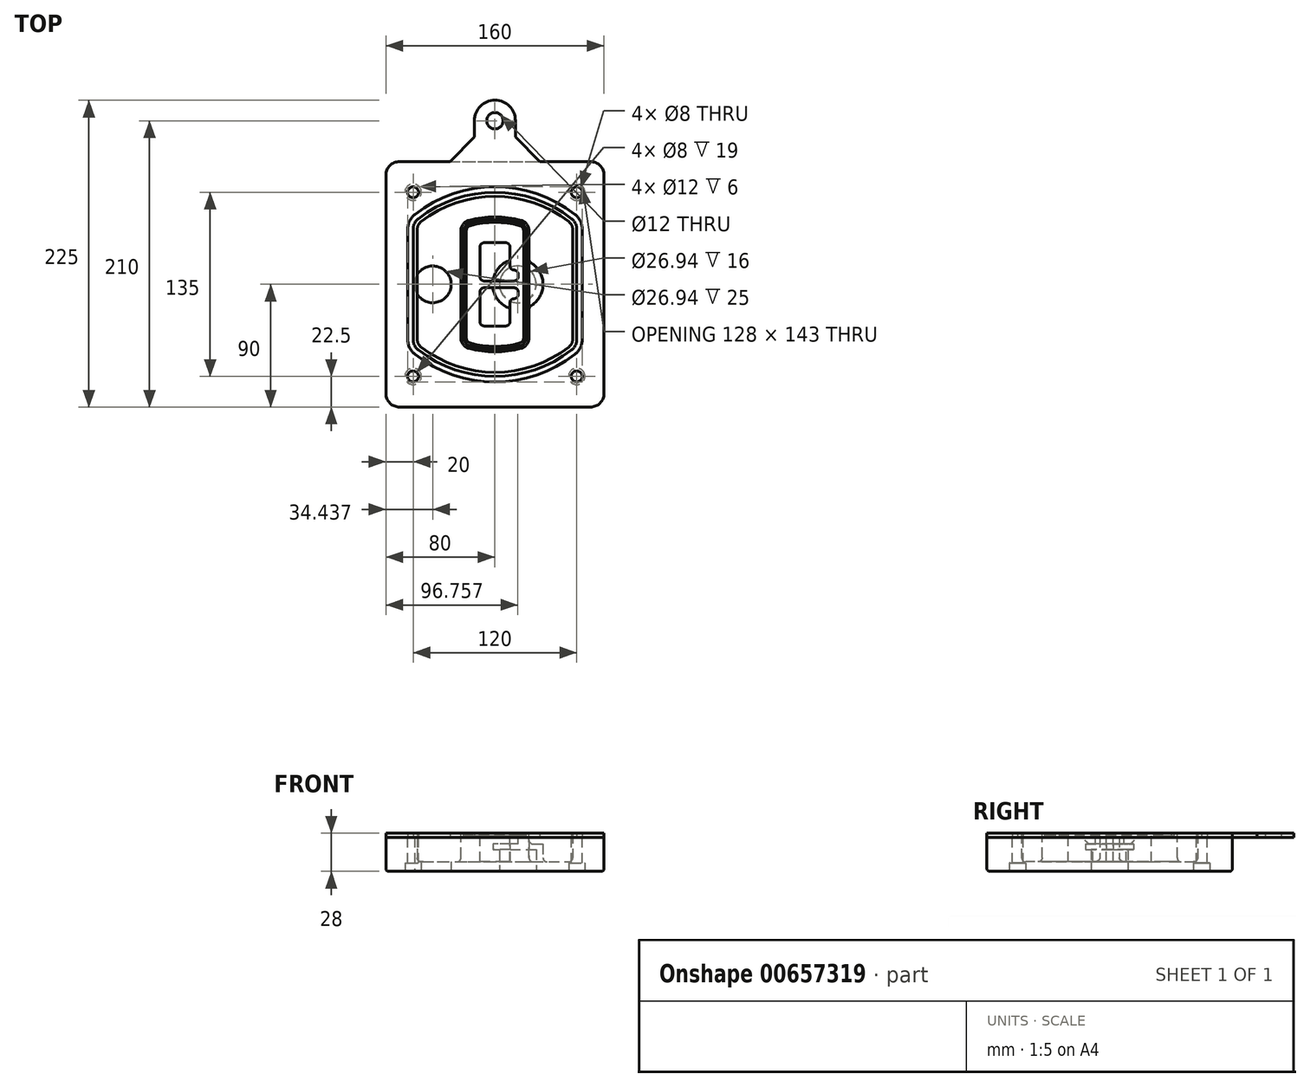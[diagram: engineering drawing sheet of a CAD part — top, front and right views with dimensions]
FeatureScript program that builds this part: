
annotation { "Feature Type Name" : "Feature", "Feature Type Description" : "" }
export const myFeature = defineFeature(function(context is Context, id is Id, definition is map)
    precondition{}
    {
        {
            var Q0;
            Q0=qCreatedBy(makeId("Top.planeOp"),FACE);
            var sketch = newSketch(context, id + "F0", { "sketchPlane" : qUnion([Q0])});
            skPoint(sketch, "E0.rect.middle", {"position": v(0, 0) * mm});
            skLineSegment(sketch, "E1.bottom", {"start": v(-70, -90) * mm, "end": v(70, -90) * mm});
            skLineSegment(sketch, "E1.top", {"start": v(-70, 90) * mm, "end": v(70, 90) * mm});
            skLineSegment(sketch, "E1.left", {"start": v(-80, -80) * mm, "end": v(-80, 80) * mm});
            skLineSegment(sketch, "E1.right", {"start": v(80, -80) * mm, "end": v(80, 80) * mm});
            skLineSegment(sketch, "E2", {"start": v(-80, 90) * mm, "end": v(80, -90) * mm, "construction": true});
            skLineSegment(sketch, "E3", {"start": v(80, 90) * mm, "end": v(-80, -90) * mm, "construction": true});
            skCircle(sketch, "E4", {"center": v(-60, 67.5) * mm, "radius": 4 * mm});
            skCircle(sketch, "E5", {"center": v(60, 67.5) * mm, "radius": 4 * mm});
            skCircle(sketch, "E6", {"center": v(60, -67.5) * mm, "radius": 4 * mm});
            skCircle(sketch, "E7", {"center": v(-60, -67.5) * mm, "radius": 4 * mm});
            skLineSegment(sketch, "E8", {"start": v(-60, 67.5) * mm, "end": v(60, 67.5) * mm, "construction": true});
            skLineSegment(sketch, "E9", {"start": v(60, 67.5) * mm, "end": v(60, -67.5) * mm, "construction": true});
            skLineSegment(sketch, "E10", {"start": v(60, -67.5) * mm, "end": v(-60, -67.5) * mm, "construction": true});
            skLineSegment(sketch, "E11", {"start": v(-60, -67.5) * mm, "end": v(-60, 67.5) * mm, "construction": true});
            skLineSegment(sketch, "E12", {"start": v(-60, 40.3) * mm, "end": v(-60, -40.3) * mm});
            skLineSegment(sketch, "E13", {"start": v(60, 40.3) * mm, "end": v(60, -40.3) * mm});
            skArc(sketch, "E14", {"start": v(56.15, 48.18) * mm, "mid": v(0, 67.5) * mm, "end": v(-56.15, 48.18) * mm});
            skArc(sketch, "E15", {"start": v(-56.15, -48.18) * mm, "mid": v(0, -67.5) * mm, "end": v(56.15, -48.18) * mm});
            skLineSegment(sketch, "E16", {"start": v(-60, 0) * mm, "end": v(60, 0) * mm, "construction": true});
            skPoint(sketch, "E17.visualSharp", {"position": v(-60, -45) * mm});
            skArc(sketch, "E17.filletArc", {"start": v(-60, -40.3) * mm, "mid": v(-58.99, -44.68) * mm, "end": v(-56.15, -48.18) * mm});
            skPoint(sketch, "E18.visualSharp", {"position": v(-60, 45) * mm});
            skArc(sketch, "E18.filletArc", {"start": v(-56.15, 48.18) * mm, "mid": v(-58.99, 44.68) * mm, "end": v(-60, 40.3) * mm});
            skPoint(sketch, "E19.visualSharp", {"position": v(60, 45) * mm});
            skArc(sketch, "E19.filletArc", {"start": v(60, 40.3) * mm, "mid": v(58.99, 44.68) * mm, "end": v(56.15, 48.18) * mm});
            skPoint(sketch, "E20.visualSharp", {"position": v(60, -45) * mm});
            skArc(sketch, "E20.filletArc", {"start": v(56.15, -48.18) * mm, "mid": v(58.99, -44.68) * mm, "end": v(60, -40.3) * mm});
            skPoint(sketch, "E21.visualSharp", {"position": v(-80, 90) * mm});
            skArc(sketch, "E21.filletArc", {"start": v(-70, 90) * mm, "mid": v(-77.07, 87.07) * mm, "end": v(-80, 80) * mm});
            skPoint(sketch, "E22.visualSharp", {"position": v(80, 90) * mm});
            skArc(sketch, "E22.filletArc", {"start": v(80, 80) * mm, "mid": v(77.07, 87.07) * mm, "end": v(70, 90) * mm});
            skPoint(sketch, "E23.visualSharp", {"position": v(80, -90) * mm});
            skArc(sketch, "E23.filletArc", {"start": v(70, -90) * mm, "mid": v(77.07, -87.07) * mm, "end": v(80, -80) * mm});
            skPoint(sketch, "E24.visualSharp", {"position": v(-80, -90) * mm});
            skArc(sketch, "E24.filletArc", {"start": v(-80, -80) * mm, "mid": v(-77.07, -87.07) * mm, "end": v(-70, -90) * mm});
            skArc(sketch, "E25.0", {"start": v(57, 40.3) * mm, "mid": v(56.3, 43.36) * mm, "end": v(54.3, 45.81) * mm});
            skLineSegment(sketch, "E25.1", {"start": v(57, 40.3) * mm, "end": v(57, -40.3) * mm});
            skArc(sketch, "E25.2", {"start": v(54.3, -45.81) * mm, "mid": v(56.3, -43.36) * mm, "end": v(57, -40.3) * mm});
            skArc(sketch, "E25.3", {"start": v(-54.3, -45.81) * mm, "mid": v(0, -64.5) * mm, "end": v(54.3, -45.81) * mm});
            skArc(sketch, "E25.4", {"start": v(-57, -40.3) * mm, "mid": v(-56.3, -43.36) * mm, "end": v(-54.3, -45.81) * mm});
            skArc(sketch, "E25.5", {"start": v(54.3, 45.81) * mm, "mid": v(0, 64.5) * mm, "end": v(-54.3, 45.81) * mm});
            skLineSegment(sketch, "E25.6", {"start": v(-57, 40.3) * mm, "end": v(-57, -40.3) * mm});
            skArc(sketch, "E25.7", {"start": v(-54.3, 45.81) * mm, "mid": v(-56.3, 43.36) * mm, "end": v(-57, 40.3) * mm});
            skArc(sketch, "E26.0", {"start": v(-58.62, 51.33) * mm, "mid": v(-62.58, 46.43) * mm, "end": v(-64, 40.3) * mm});
            skArc(sketch, "E26.1", {"start": v(58.62, 51.33) * mm, "mid": v(0, 71.5) * mm, "end": v(-58.62, 51.33) * mm});
            skArc(sketch, "E26.2", {"start": v(64, 40.3) * mm, "mid": v(62.58, 46.43) * mm, "end": v(58.62, 51.33) * mm});
            skLineSegment(sketch, "E26.3", {"start": v(64, 40.3) * mm, "end": v(64, -40.3) * mm});
            skArc(sketch, "E26.4", {"start": v(58.62, -51.33) * mm, "mid": v(62.58, -46.43) * mm, "end": v(64, -40.3) * mm});
            skLineSegment(sketch, "E26.5", {"start": v(-64, 40.3) * mm, "end": v(-64, -40.3) * mm});
            skArc(sketch, "E26.6", {"start": v(-58.62, -51.33) * mm, "mid": v(0, -71.5) * mm, "end": v(58.62, -51.33) * mm});
            skArc(sketch, "E26.7", {"start": v(-64, -40.3) * mm, "mid": v(-62.58, -46.43) * mm, "end": v(-58.62, -51.33) * mm});
            skLineSegment(sketch, "E27", {"start": v(0, 90) * mm, "end": v(0, 120) * mm, "construction": true});
            skCircle(sketch, "E28", {"center": v(0, 120) * mm, "radius": 6 * mm});
            skLineSegment(sketch, "E29", {"start": v(-33, 90) * mm, "end": v(-15, 108) * mm});
            skLineSegment(sketch, "E30", {"start": v(33, 90) * mm, "end": v(15, 108) * mm});
            skLineSegment(sketch, "E31", {"start": v(-15, 108) * mm, "end": v(-15, 120) * mm});
            skLineSegment(sketch, "E32", {"start": v(15, 108) * mm, "end": v(15, 120) * mm});
            skArc(sketch, "E33", {"start": v(15, 120) * mm, "mid": v(0, 135) * mm, "end": v(-15, 120) * mm});
            skLineSegment(sketch, "E34", {"start": v(-80, 0) * mm, "end": v(80, 0) * mm, "construction": true});
            skSolve(sketch);
        }
        {
            var Q0;
            Q0=makeQuery(id+"F0.imprint","IMPRINT",FACE,{"disambiguationData":[TD([[makeQuery(id+"F0.imprint","IMPRINT",EDGE,{"derivedFrom":sQuery(id+"F0.wireOp",EDGE,"E1.bottom")}),1.0]])]});
            var Q1;
            Q1=makeQuery(id+"F0.imprint","IMPRINT",FACE,{"disambiguationData":[TD([[makeQuery(id+"F0.imprint","IMPRINT",EDGE,{"derivedFrom":sQuery(id+"F0.wireOp",EDGE,"E12")}),1.0]])]});
            var Q2;
            Q2=makeQuery(id+"F0.imprint","IMPRINT",FACE,{"disambiguationData":[TD([[makeQuery(id+"F0.imprint","IMPRINT",EDGE,{"derivedFrom":sQuery(id+"F0.wireOp",EDGE,"E25.0")}),1.0]])]});
            var Q3;
            Q3=makeQuery(id+"F0.imprint","IMPRINT",FACE,{"disambiguationData":[TD([[makeQuery(id+"F0.imprint","IMPRINT",EDGE,{"derivedFrom":sQuery(id+"F0.wireOp",EDGE,"E12")}),-1.0]])]});
            extrude(context, id + "F1", {"entities" : qUnion([Q0, Q1, Q2, Q3]), "oppositeDirection" : true, "depth" : 25 * mm});
        }
        {
            var Q0;
            Q0=makeQuery(id+"F0.imprint","IMPRINT",FACE,{"disambiguationData":[TD([[makeQuery(id+"F0.imprint","IMPRINT",EDGE,{"derivedFrom":sQuery(id+"F0.wireOp",EDGE,"E12")}),1.0]])]});
            extrude(context, id + "F2", {"entities" : qUnion([Q0]), "operationType" : NewBodyOperationType.ADD, "depth" : 3 * mm});
        }
        {
            var Q0;
            Q0=makeQuery(id+"F0.imprint","IMPRINT",FACE,{"disambiguationData":[TD([[makeQuery(id+"F0.imprint","IMPRINT",EDGE,{"derivedFrom":sQuery(id+"F0.wireOp",EDGE,"E25.0")}),1.0]])]});
            extrude(context, id + "F3", {"entities" : qUnion([Q0]), "operationType" : NewBodyOperationType.REMOVE, "oppositeDirection" : true, "depth" : 18 * mm});
        }
        {
            var Q0;
            Q0=makeQuery(id+"F2.opExtrude","CAP_FACE",FACE,{"disambiguationData":[OSD([sQuery(id+"F0.wireOp",EDGE,"E12"),sQuery(id+"F0.wireOp",EDGE,"E13"),sQuery(id+"F0.wireOp",EDGE,"E14"),sQuery(id+"F0.wireOp",EDGE,"E15"),sQuery(id+"F0.wireOp",EDGE,"E17.filletArc"),sQuery(id+"F0.wireOp",EDGE,"E18.filletArc"),sQuery(id+"F0.wireOp",EDGE,"E19.filletArc"),sQuery(id+"F0.wireOp",EDGE,"E20.filletArc"),sQuery(id+"F0.wireOp",EDGE,"E25.0"),sQuery(id+"F0.wireOp",EDGE,"E25.1"),sQuery(id+"F0.wireOp",EDGE,"E25.2"),sQuery(id+"F0.wireOp",EDGE,"E25.3"),sQuery(id+"F0.wireOp",EDGE,"E25.4"),sQuery(id+"F0.wireOp",EDGE,"E25.5"),sQuery(id+"F0.wireOp",EDGE,"E25.6"),sQuery(id+"F0.wireOp",EDGE,"E25.7")])],"isStart":false});
            var sketch = newSketch(context, id + "F4", { "sketchPlane" : qUnion([Q0])});
            skArc(sketch, "E35.0", {"start": v(-19.08, -46.97) * mm, "mid": v(0, -49.5) * mm, "end": v(19.08, -46.97) * mm});
            skArc(sketch, "E36.0", {"start": v(19.08, 46.97) * mm, "mid": v(0, 49.5) * mm, "end": v(-19.08, 46.97) * mm});
            skLineSegment(sketch, "E37", {"start": v(-25, 39.25) * mm, "end": v(-25, -39.25) * mm});
            skLineSegment(sketch, "E38", {"start": v(25, 39.25) * mm, "end": v(25, -39.25) * mm});
            skLineSegment(sketch, "E39", {"start": v(-25, 45.1) * mm, "end": v(25, 45.1) * mm, "construction": true});
            skLineSegment(sketch, "E40", {"start": v(-25, -45.1) * mm, "end": v(25, -45.1) * mm, "construction": true});
            skPoint(sketch, "E41.visualSharp", {"position": v(-25, 45.1) * mm});
            skArc(sketch, "E41.filletArc", {"start": v(-19.08, 46.97) * mm, "mid": v(-23.35, 44.11) * mm, "end": v(-25, 39.25) * mm});
            skPoint(sketch, "E42.visualSharp", {"position": v(25, 45.1) * mm});
            skArc(sketch, "E42.filletArc", {"start": v(25, 39.25) * mm, "mid": v(23.35, 44.11) * mm, "end": v(19.08, 46.97) * mm});
            skPoint(sketch, "E43.visualSharp", {"position": v(25, -45.1) * mm});
            skArc(sketch, "E43.filletArc", {"start": v(19.08, -46.97) * mm, "mid": v(23.35, -44.11) * mm, "end": v(25, -39.25) * mm});
            skPoint(sketch, "E44.visualSharp", {"position": v(-25, -45.1) * mm});
            skArc(sketch, "E44.filletArc", {"start": v(-25, -39.25) * mm, "mid": v(-23.35, -44.11) * mm, "end": v(-19.08, -46.97) * mm});
            skArc(sketch, "E45.0", {"start": v(54.3, 45.81) * mm, "mid": v(0, 64.5) * mm, "end": v(-54.3, 45.81) * mm});
            skArc(sketch, "E45.1", {"start": v(-54.3, 45.81) * mm, "mid": v(-56.3, 43.36) * mm, "end": v(-57, 40.3) * mm});
            skLineSegment(sketch, "E45.2", {"start": v(-57, 40.3) * mm, "end": v(-57, -40.3) * mm});
            skArc(sketch, "E45.3", {"start": v(-57, -40.3) * mm, "mid": v(-56.3, -43.36) * mm, "end": v(-54.3, -45.81) * mm});
            skArc(sketch, "E45.4", {"start": v(-54.3, -45.81) * mm, "mid": v(0, -64.5) * mm, "end": v(54.3, -45.81) * mm});
            skArc(sketch, "E45.5", {"start": v(54.3, -45.81) * mm, "mid": v(56.3, -43.36) * mm, "end": v(57, -40.3) * mm});
            skLineSegment(sketch, "E45.6", {"start": v(57, 40.3) * mm, "end": v(57, -40.3) * mm});
            skArc(sketch, "E45.7", {"start": v(57, 40.3) * mm, "mid": v(56.3, 43.36) * mm, "end": v(54.3, 45.81) * mm});
            skLineSegment(sketch, "E46.0", {"start": v(23, 39.25) * mm, "end": v(23, -39.25) * mm});
            skArc(sketch, "E46.1", {"start": v(18.56, -45.04) * mm, "mid": v(21.76, -42.9) * mm, "end": v(23, -39.25) * mm});
            skArc(sketch, "E46.2", {"start": v(-18.56, -45.04) * mm, "mid": v(0, -47.5) * mm, "end": v(18.56, -45.04) * mm});
            skArc(sketch, "E46.3", {"start": v(-23, -39.25) * mm, "mid": v(-21.76, -42.9) * mm, "end": v(-18.56, -45.04) * mm});
            skLineSegment(sketch, "E46.4", {"start": v(-23, 39.25) * mm, "end": v(-23, -39.25) * mm});
            skArc(sketch, "E46.5", {"start": v(23, 39.25) * mm, "mid": v(21.76, 42.9) * mm, "end": v(18.56, 45.04) * mm});
            skArc(sketch, "E46.6", {"start": v(-18.56, 45.04) * mm, "mid": v(-21.76, 42.9) * mm, "end": v(-23, 39.25) * mm});
            skArc(sketch, "E46.7", {"start": v(18.56, 45.04) * mm, "mid": v(0, 47.5) * mm, "end": v(-18.56, 45.04) * mm});
            skArc(sketch, "E47.0", {"start": v(21, 39.25) * mm, "mid": v(20.18, 41.68) * mm, "end": v(18.04, 43.1) * mm});
            skLineSegment(sketch, "E47.1", {"start": v(21, 39.25) * mm, "end": v(21, -39.25) * mm});
            skArc(sketch, "E47.2", {"start": v(18.04, -43.1) * mm, "mid": v(20.18, -41.68) * mm, "end": v(21, -39.25) * mm});
            skArc(sketch, "E47.3", {"start": v(-18.04, -43.1) * mm, "mid": v(0, -45.5) * mm, "end": v(18.04, -43.1) * mm});
            skArc(sketch, "E47.4", {"start": v(-21, -39.25) * mm, "mid": v(-20.18, -41.68) * mm, "end": v(-18.04, -43.1) * mm});
            skArc(sketch, "E47.5", {"start": v(18.04, 43.1) * mm, "mid": v(0, 45.5) * mm, "end": v(-18.04, 43.1) * mm});
            skLineSegment(sketch, "E47.6", {"start": v(-21, 39.25) * mm, "end": v(-21, -39.25) * mm});
            skArc(sketch, "E47.7", {"start": v(-18.04, 43.1) * mm, "mid": v(-20.18, 41.68) * mm, "end": v(-21, 39.25) * mm});
            skLineSegment(sketch, "E48", {"start": v(-25, 0) * mm, "end": v(25, 0) * mm, "construction": true});
            skLineSegment(sketch, "E49", {"start": v(-11, 5.5) * mm, "end": v(-11, 27.5) * mm});
            skLineSegment(sketch, "E50", {"start": v(-8, 30.5) * mm, "end": v(8, 30.5) * mm});
            skLineSegment(sketch, "E51", {"start": v(11, 27.5) * mm, "end": v(11, 13.5) * mm});
            skLineSegment(sketch, "E52", {"start": v(14, 10.5) * mm, "end": v(14, 10.5) * mm});
            skLineSegment(sketch, "E53", {"start": v(17, 7.5) * mm, "end": v(17, 5.5) * mm});
            skLineSegment(sketch, "E54", {"start": v(14, 2.5) * mm, "end": v(-8, 2.5) * mm});
            skPoint(sketch, "E55.visualSharp", {"position": v(-11, 30.5) * mm});
            skArc(sketch, "E55.filletArc", {"start": v(-8, 30.5) * mm, "mid": v(-10.12, 29.62) * mm, "end": v(-11, 27.5) * mm});
            skPoint(sketch, "E56.visualSharp", {"position": v(11, 30.5) * mm});
            skArc(sketch, "E56.filletArc", {"start": v(11, 27.5) * mm, "mid": v(10.12, 29.62) * mm, "end": v(8, 30.5) * mm});
            skPoint(sketch, "E57.visualSharp", {"position": v(11, 10.5) * mm});
            skArc(sketch, "E57.filletArc", {"start": v(11, 13.5) * mm, "mid": v(11.88, 11.38) * mm, "end": v(14, 10.5) * mm});
            skPoint(sketch, "E58.visualSharp", {"position": v(17, 10.5) * mm});
            skArc(sketch, "E58.filletArc", {"start": v(17, 7.5) * mm, "mid": v(16.12, 9.62) * mm, "end": v(14, 10.5) * mm});
            skPoint(sketch, "E59.visualSharp", {"position": v(17, 2.5) * mm});
            skArc(sketch, "E59.filletArc", {"start": v(14, 2.5) * mm, "mid": v(16.12, 3.38) * mm, "end": v(17, 5.5) * mm});
            skPoint(sketch, "E60.visualSharp", {"position": v(-11, 2.5) * mm});
            skArc(sketch, "E60.filletArc", {"start": v(-11, 5.5) * mm, "mid": v(-10.12, 3.38) * mm, "end": v(-8, 2.5) * mm});
            skLineSegment(sketch, "E61.0.MirrorCS", {"start": v(14, -2.5) * mm, "end": v(-8, -2.5) * mm});
            skArc(sketch, "E62.0.MirrorCS", {"start": v(-11, -5.5) * mm, "mid": v(-10.12, -3.38) * mm, "end": v(-8, -2.5) * mm});
            skLineSegment(sketch, "E63.0.MirrorCS", {"start": v(-11, -5.5) * mm, "end": v(-11, -27.5) * mm});
            skArc(sketch, "E64.0.MirrorCS", {"start": v(-8, -30.5) * mm, "mid": v(-10.12, -29.62) * mm, "end": v(-11, -27.5) * mm});
            skLineSegment(sketch, "E65.0.MirrorCS", {"start": v(-8, -30.5) * mm, "end": v(8, -30.5) * mm});
            skArc(sketch, "E66.0.MirrorCS", {"start": v(11, -27.5) * mm, "mid": v(10.12, -29.62) * mm, "end": v(8, -30.5) * mm});
            skLineSegment(sketch, "E67.0.MirrorCS", {"start": v(11, -27.5) * mm, "end": v(11, -13.5) * mm});
            skArc(sketch, "E68.0.MirrorCS", {"start": v(11, -13.5) * mm, "mid": v(11.88, -11.38) * mm, "end": v(14, -10.5) * mm});
            skArc(sketch, "E69.0.MirrorCS", {"start": v(17, -7.5) * mm, "mid": v(16.12, -9.62) * mm, "end": v(14, -10.5) * mm});
            skLineSegment(sketch, "E70.0.MirrorCS", {"start": v(17, -7.5) * mm, "end": v(17, -5.5) * mm});
            skArc(sketch, "E71.0.MirrorCS", {"start": v(14, -2.5) * mm, "mid": v(16.12, -3.38) * mm, "end": v(17, -5.5) * mm});
            skSolve(sketch);
        }
        {
            var Q0;
            Q0=makeQuery(id+"F4.imprint","IMPRINT",FACE,{"disambiguationData":[TD([[makeQuery(id+"F4.imprint","IMPRINT",EDGE,{"derivedFrom":sQuery(id+"F4.wireOp",EDGE,"E35.0")}),1.0]])]});
            var Q1;
            Q1=makeQuery(id+"F4.imprint","IMPRINT",FACE,{"disambiguationData":[TD([[makeQuery(id+"F4.imprint","IMPRINT",EDGE,{"derivedFrom":sQuery(id+"F4.wireOp",EDGE,"E46.0")}),-1.0]])]});
            var Q2;
            Q2=makeQuery(id+"F4.imprint","IMPRINT",FACE,{"disambiguationData":[TD([[makeQuery(id+"F4.imprint","IMPRINT",EDGE,{"derivedFrom":sQuery(id+"F4.wireOp",EDGE,"E47.0")}),1.0]])]});
            extrude(context, id + "F5", {"entities" : qUnion([Q0, Q1, Q2]), "operationType" : NewBodyOperationType.ADD, "endBound" : BoundingType.UP_TO_NEXT, "oppositeDirection" : true, "depth" : 25 * mm});
        }
        {
            var Q0;
            Q0=makeQuery(id+"F4.imprint","IMPRINT",FACE,{"disambiguationData":[TD([[makeQuery(id+"F4.imprint","IMPRINT",EDGE,{"derivedFrom":sQuery(id+"F4.wireOp",EDGE,"E46.0")}),-1.0]])]});
            extrude(context, id + "F6", {"entities" : qUnion([Q0]), "operationType" : NewBodyOperationType.REMOVE, "oppositeDirection" : true, "depth" : 2 * mm});
        }
        {
            var Q0;
            Q0=makeQuery(id+"F1.opExtrude","CAP_FACE",FACE,{"disambiguationData":[OSD([sQuery(id+"F0.wireOp",EDGE,"E1.bottom"),sQuery(id+"F0.wireOp",EDGE,"E1.top"),sQuery(id+"F0.wireOp",EDGE,"E1.left"),sQuery(id+"F0.wireOp",EDGE,"E1.right"),sQuery(id+"F0.wireOp",EDGE,"E4"),sQuery(id+"F0.wireOp",EDGE,"E5"),sQuery(id+"F0.wireOp",EDGE,"E6"),sQuery(id+"F0.wireOp",EDGE,"E7"),sQuery(id+"F0.wireOp",EDGE,"E21.filletArc"),sQuery(id+"F0.wireOp",EDGE,"E22.filletArc"),sQuery(id+"F0.wireOp",EDGE,"E23.filletArc"),sQuery(id+"F0.wireOp",EDGE,"E24.filletArc")])],"isStart":false});
            var sketch = newSketch(context, id + "F7", { "sketchPlane" : qUnion([Q0])});
            skCircle(sketch, "E72", {"center": v(16.76, 0) * mm, "radius": 13.47 * mm});
            skCircle(sketch, "E73", {"center": v(-45.56, 0) * mm, "radius": 13.47 * mm});
            skLineSegment(sketch, "E74", {"start": v(80, 0) * mm, "end": v(-80, 0) * mm});
            skCircle(sketch, "E75", {"center": v(16.76, 0) * mm, "radius": 18.47 * mm});
            skCircle(sketch, "E76", {"center": v(60, -67.5) * mm, "radius": 6 * mm});
            skCircle(sketch, "E77", {"center": v(-60, -67.5) * mm, "radius": 6 * mm});
            skCircle(sketch, "E78", {"center": v(-60, 67.5) * mm, "radius": 6 * mm});
            skCircle(sketch, "E79", {"center": v(60, 67.5) * mm, "radius": 6 * mm});
            skSolve(sketch);
        }
        {
            var Q0;
            {var subQ1=sQuery(id+"F7.wireOp",EDGE,"E74");var subQ4=sQuery(id+"F7.wireOp",EDGE,"E72");var subQ6=makeQuery(id+"F7.imprint","INTERSECT",VERTEX,{"disambiguationData":[OD(0.0)],"derivedFrom":[subQ4,subQ1]});Q0=makeQuery(id+"F7.imprint","IMPRINT",FACE,{"disambiguationData":[TD([[makeQuery(id+"F7.imprint","IMPRINT",EDGE,{"disambiguationData":[TD([[subQ6,-1.0]])],"derivedFrom":subQ4}),-1.0]])]});}
            var Q1;
            {var subQ0=sQuery(id+"F7.wireOp",EDGE,"E74");var subQ1=sQuery(id+"F7.wireOp",EDGE,"E72");var subQ3=makeQuery(id+"F7.imprint","INTERSECT",VERTEX,{"disambiguationData":[OD(0.0)],"derivedFrom":[subQ1,subQ0]});Q1=makeQuery(id+"F7.imprint","IMPRINT",FACE,{"disambiguationData":[TD([[makeQuery(id+"F7.imprint","IMPRINT",EDGE,{"disambiguationData":[TD([[subQ3,-1.0]])],"derivedFrom":subQ1}),1.0]])]});}
            var Q2;
            {var subQ0=sQuery(id+"F7.wireOp",EDGE,"E74");var subQ1=sQuery(id+"F7.wireOp",EDGE,"E72");var subQ3=makeQuery(id+"F7.imprint","INTERSECT",VERTEX,{"disambiguationData":[OD(0.0)],"derivedFrom":[subQ1,subQ0]});Q2=makeQuery(id+"F7.imprint","IMPRINT",FACE,{"disambiguationData":[TD([[makeQuery(id+"F7.imprint","IMPRINT",EDGE,{"disambiguationData":[TD([[subQ3,1.0]])],"derivedFrom":subQ1}),1.0]])]});}
            var Q3;
            {var subQ1=sQuery(id+"F7.wireOp",EDGE,"E74");var subQ4=sQuery(id+"F7.wireOp",EDGE,"E72");var subQ6=makeQuery(id+"F7.imprint","INTERSECT",VERTEX,{"disambiguationData":[OD(0.0)],"derivedFrom":[subQ4,subQ1]});Q3=makeQuery(id+"F7.imprint","IMPRINT",FACE,{"disambiguationData":[TD([[makeQuery(id+"F7.imprint","IMPRINT",EDGE,{"disambiguationData":[TD([[subQ6,1.0]])],"derivedFrom":subQ4}),-1.0]])]});}
            extrude(context, id + "F8", {"entities" : qUnion([Q0, Q1, Q2, Q3]), "operationType" : NewBodyOperationType.ADD, "oppositeDirection" : true, "depth" : 20 * mm});
        }
        {
            var Q0;
            {var subQ0=sQuery(id+"F7.wireOp",EDGE,"E74");var subQ1=sQuery(id+"F7.wireOp",EDGE,"E72");var subQ3=makeQuery(id+"F7.imprint","INTERSECT",VERTEX,{"disambiguationData":[OD(0.0)],"derivedFrom":[subQ1,subQ0]});Q0=makeQuery(id+"F7.imprint","IMPRINT",FACE,{"disambiguationData":[TD([[makeQuery(id+"F7.imprint","IMPRINT",EDGE,{"disambiguationData":[TD([[subQ3,-1.0]])],"derivedFrom":subQ1}),1.0]])]});}
            var Q1;
            {var subQ0=sQuery(id+"F7.wireOp",EDGE,"E74");var subQ1=sQuery(id+"F7.wireOp",EDGE,"E72");var subQ3=makeQuery(id+"F7.imprint","INTERSECT",VERTEX,{"disambiguationData":[OD(0.0)],"derivedFrom":[subQ1,subQ0]});Q1=makeQuery(id+"F7.imprint","IMPRINT",FACE,{"disambiguationData":[TD([[makeQuery(id+"F7.imprint","IMPRINT",EDGE,{"disambiguationData":[TD([[subQ3,1.0]])],"derivedFrom":subQ1}),1.0]])]});}
            extrude(context, id + "F9", {"entities" : qUnion([Q0, Q1]), "operationType" : NewBodyOperationType.REMOVE, "oppositeDirection" : true, "depth" : 16 * mm});
        }
        {
            var Q0;
            {var subQ0=sQuery(id+"F7.wireOp",EDGE,"E74");var subQ1=sQuery(id+"F7.wireOp",EDGE,"E73");var subQ3=makeQuery(id+"F7.imprint","INTERSECT",VERTEX,{"disambiguationData":[OD(0.0)],"derivedFrom":[subQ1,subQ0]});Q0=makeQuery(id+"F7.imprint","IMPRINT",FACE,{"disambiguationData":[TD([[makeQuery(id+"F7.imprint","IMPRINT",EDGE,{"disambiguationData":[TD([[subQ3,-1.0]])],"derivedFrom":subQ1}),1.0]])]});}
            var Q1;
            {var subQ0=sQuery(id+"F7.wireOp",EDGE,"E74");var subQ1=sQuery(id+"F7.wireOp",EDGE,"E73");var subQ3=makeQuery(id+"F7.imprint","INTERSECT",VERTEX,{"disambiguationData":[OD(0.0)],"derivedFrom":[subQ1,subQ0]});Q1=makeQuery(id+"F7.imprint","IMPRINT",FACE,{"disambiguationData":[TD([[makeQuery(id+"F7.imprint","IMPRINT",EDGE,{"disambiguationData":[TD([[subQ3,1.0]])],"derivedFrom":subQ1}),1.0]])]});}
            extrude(context, id + "F10", {"entities" : qUnion([Q0, Q1]), "operationType" : NewBodyOperationType.REMOVE, "oppositeDirection" : true, "depth" : 25 * mm});
        }
        {
            var Q0;
            Q0=makeQuery(id+"F7.imprint","IMPRINT",FACE,{"disambiguationData":[TD([[makeQuery(id+"F7.imprint","IMPRINT",EDGE,{"derivedFrom":sQuery(id+"F7.wireOp",EDGE,"E76")}),1.0]])]});
            var Q1;
            Q1=makeQuery(id+"F7.imprint","IMPRINT",FACE,{"disambiguationData":[TD([[makeQuery(id+"F7.imprint","IMPRINT",EDGE,{"derivedFrom":makeQuery(id+"F1.opExtrude","CAP_EDGE",EDGE,{"disambiguationData":[OSD([sQuery(id+"F0.wireOp",EDGE,"E5")])],"isStart":false})}),-1.0]])]});
            var Q2;
            Q2=makeQuery(id+"F7.imprint","IMPRINT",FACE,{"disambiguationData":[TD([[makeQuery(id+"F7.imprint","IMPRINT",EDGE,{"derivedFrom":sQuery(id+"F7.wireOp",EDGE,"E77")}),1.0]])]});
            var Q3;
            Q3=makeQuery(id+"F7.imprint","IMPRINT",FACE,{"disambiguationData":[TD([[makeQuery(id+"F7.imprint","IMPRINT",EDGE,{"derivedFrom":makeQuery(id+"F1.opExtrude","CAP_EDGE",EDGE,{"disambiguationData":[OSD([sQuery(id+"F0.wireOp",EDGE,"E4")])],"isStart":false})}),-1.0]])]});
            var Q4;
            Q4=makeQuery(id+"F7.imprint","IMPRINT",FACE,{"disambiguationData":[TD([[makeQuery(id+"F7.imprint","IMPRINT",EDGE,{"derivedFrom":sQuery(id+"F7.wireOp",EDGE,"E78")}),1.0]])]});
            var Q5;
            Q5=makeQuery(id+"F7.imprint","IMPRINT",FACE,{"disambiguationData":[TD([[makeQuery(id+"F7.imprint","IMPRINT",EDGE,{"derivedFrom":makeQuery(id+"F1.opExtrude","CAP_EDGE",EDGE,{"disambiguationData":[OSD([sQuery(id+"F0.wireOp",EDGE,"E7")])],"isStart":false})}),-1.0]])]});
            var Q6;
            Q6=makeQuery(id+"F7.imprint","IMPRINT",FACE,{"disambiguationData":[TD([[makeQuery(id+"F7.imprint","IMPRINT",EDGE,{"derivedFrom":sQuery(id+"F7.wireOp",EDGE,"E79")}),1.0]])]});
            var Q7;
            Q7=makeQuery(id+"F7.imprint","IMPRINT",FACE,{"disambiguationData":[TD([[makeQuery(id+"F7.imprint","IMPRINT",EDGE,{"derivedFrom":makeQuery(id+"F1.opExtrude","CAP_EDGE",EDGE,{"disambiguationData":[OSD([sQuery(id+"F0.wireOp",EDGE,"E6")])],"isStart":false})}),-1.0]])]});
            extrude(context, id + "F11", {"entities" : qUnion([Q0, Q1, Q2, Q3, Q4, Q5, Q6, Q7]), "operationType" : NewBodyOperationType.REMOVE, "oppositeDirection" : true, "depth" : 6 * mm});
        }
        {
            var Q0;
            Q0=makeQuery(id+"F9.boolean.opBoolean","COPY",FACE,{"derivedFrom":makeQuery(id+"F9.opExtrude","CAP_FACE",FACE,{"disambiguationData":[OSD([sQuery(id+"F7.wireOp",EDGE,"E72")])],"isStart":false})});
            var sketch = newSketch(context, id + "F12", { "sketchPlane" : qUnion([Q0])});
            skArc(sketch, "E80.0", {"start": v(11, 17.55) * mm, "mid": v(2.57, 11.82) * mm, "end": v(-1.54, 2.5) * mm});
            skArc(sketch, "E80.1", {"start": v(-1.54, -2.5) * mm, "mid": v(2.57, -11.82) * mm, "end": v(11, -17.55) * mm});
            skLineSegment(sketch, "E81", {"start": v(-1.54, -2.5) * mm, "end": v(14, -2.5) * mm});
            skLineSegment(sketch, "E82.0", {"start": v(14, 2.5) * mm, "end": v(-1.54, 2.5) * mm});
            skArc(sketch, "E82.1", {"start": v(14, 2.5) * mm, "mid": v(16.12, 3.38) * mm, "end": v(17, 5.5) * mm});
            skLineSegment(sketch, "E82.2", {"start": v(17, 7.5) * mm, "end": v(17, 5.5) * mm});
            skArc(sketch, "E82.3", {"start": v(17, 7.5) * mm, "mid": v(16.12, 9.62) * mm, "end": v(14, 10.5) * mm});
            skArc(sketch, "E82.4", {"start": v(11, 13.5) * mm, "mid": v(11.88, 11.38) * mm, "end": v(14, 10.5) * mm});
            skLineSegment(sketch, "E82.5", {"start": v(11, 17.55) * mm, "end": v(11, 13.5) * mm});
            skLineSegment(sketch, "E82.7", {"start": v(14, -2.5) * mm, "end": v(-1.54, -2.5) * mm});
            skArc(sketch, "E82.8", {"start": v(14, -2.5) * mm, "mid": v(16.12, -3.38) * mm, "end": v(17, -5.5) * mm});
            skLineSegment(sketch, "E82.9", {"start": v(17, -7.5) * mm, "end": v(17, -5.5) * mm});
            skArc(sketch, "E82.10", {"start": v(17, -7.5) * mm, "mid": v(16.12, -9.62) * mm, "end": v(14, -10.5) * mm});
            skArc(sketch, "E82.11", {"start": v(11, -13.5) * mm, "mid": v(11.88, -11.38) * mm, "end": v(14, -10.5) * mm});
            skLineSegment(sketch, "E82.12", {"start": v(11, -17.55) * mm, "end": v(11, -13.5) * mm});
            skPoint(sketch, "E83.orphan", {"position": v(11, -27.5) * mm});
            skPoint(sketch, "E84.orphan", {"position": v(-8, -2.5) * mm});
            skPoint(sketch, "E85.orphan", {"position": v(-8, 2.5) * mm});
            skPoint(sketch, "E86.orphan", {"position": v(11, 27.5) * mm});
            skSolve(sketch);
        }
        {
            var Q0;
            {var subQ7=sQuery(id+"F12.wireOp",EDGE,"E80.0");var subQ14=sQuery(id+"F12.wireOp",EDGE,"E80.1");var subQ16=sQuery(id+"F12.wireOp",EDGE,"E82.1");var subQ18=sQuery(id+"F12.wireOp",EDGE,"E82.8");Q0=qUnion([makeQuery(id+"F12.imprint","IMPRINT",FACE,{"disambiguationData":[TD([[makeQuery(id+"F12.imprint","IMPRINT",EDGE,{"derivedFrom":subQ7}),1.0]])]}),makeQuery(id+"F12.imprint","IMPRINT",FACE,{"disambiguationData":[TD([[makeQuery(id+"F12.imprint","IMPRINT",EDGE,{"derivedFrom":subQ14}),1.0]])]}),makeQuery(id+"F12.imprint","IMPRINT",FACE,{"disambiguationData":[TD([[makeQuery(id+"F12.imprint","IMPRINT",EDGE,{"derivedFrom":subQ16}),1.0]])]}),makeQuery(id+"F12.imprint","IMPRINT",FACE,{"disambiguationData":[TD([[makeQuery(id+"F12.imprint","IMPRINT",EDGE,{"derivedFrom":subQ18}),-1.0]])]})]);}
            var Q1;
            Q1=makeQuery(id+"F5.boolean.opBoolean","SPLIT",FACE,{"disambiguationData":[TD([makeQuery(id+"F5.opExtrude","SWEPT_FACE",FACE,{"disambiguationData":[OSD([sQuery(id+"F4.wireOp",EDGE,"E49")])]})])],"derivedFrom":makeQuery(id+"F3.boolean.opBoolean","COPY",FACE,{"derivedFrom":makeQuery(id+"F3.opExtrude","CAP_FACE",FACE,{"disambiguationData":[OSD([sQuery(id+"F0.wireOp",EDGE,"E25.0"),sQuery(id+"F0.wireOp",EDGE,"E25.1"),sQuery(id+"F0.wireOp",EDGE,"E25.2"),sQuery(id+"F0.wireOp",EDGE,"E25.3"),sQuery(id+"F0.wireOp",EDGE,"E25.4"),sQuery(id+"F0.wireOp",EDGE,"E25.5"),sQuery(id+"F0.wireOp",EDGE,"E25.6"),sQuery(id+"F0.wireOp",EDGE,"E25.7")])],"isStart":false})})});
            extrude(context, id + "F13", {"entities" : qUnion([Q0]), "operationType" : NewBodyOperationType.REMOVE, "endBound" : BoundingType.UP_TO_SURFACE, "endBoundEntityFace" : qUnion([Q1]), "depth" : 25 * mm});
        }
        {
            var Q0;
            Q0=makeQuery(id+"F3.boolean.opBoolean","COPY",EDGE,{"derivedFrom":makeQuery(id+"F3.opExtrude","CAP_EDGE",EDGE,{"disambiguationData":[OSD([sQuery(id+"F0.wireOp",EDGE,"E25.6")])],"isStart":false})});
            var Q1;
            Q1=makeQuery(id+"F8.boolean.opBoolean","INTERSECT",EDGE,{"derivedFrom":[makeQuery(id+"F5.opExtrude","SWEPT_FACE",FACE,{"disambiguationData":[OSD([sQuery(id+"F4.wireOp",EDGE,"E38")])]}),makeQuery(id+"F8.opExtrude","CAP_FACE",FACE,{"disambiguationData":[OSD([sQuery(id+"F7.wireOp",EDGE,"E75")])],"isStart":false})]});
            var Q2;
            Q2=makeQuery(id+"F8.boolean.opBoolean","INTERSECT",EDGE,{"disambiguationData":[OD(1.0)],"derivedFrom":[makeQuery(id+"F5.opExtrude","SWEPT_FACE",FACE,{"disambiguationData":[OSD([sQuery(id+"F4.wireOp",EDGE,"E38")])]}),makeQuery(id+"F8.opExtrude","SWEPT_FACE",FACE,{"disambiguationData":[OSD([sQuery(id+"F7.wireOp",EDGE,"E75")])]})]});
            var Q3;
            {var subQ0=sQuery(id+"F4.wireOp",EDGE,"E38");Q3=makeQuery(id+"F8.boolean.opBoolean","SPLIT",EDGE,{"disambiguationData":[TD([makeQuery(id+"F5.opExtrude","SWEPT_FACE",FACE,{"disambiguationData":[OSD([sQuery(id+"F4.wireOp",EDGE,"E43.filletArc")])]})])],"derivedFrom":makeQuery(id+"F5.opExtrude","CAP_EDGE",EDGE,{"disambiguationData":[OSD([subQ0])],"isStart":false})});}
            var Q4;
            {var subQ0=sQuery(id+"F0.wireOp",EDGE,"E25.7");var subQ1=sQuery(id+"F0.wireOp",EDGE,"E25.1");var subQ2=sQuery(id+"F0.wireOp",EDGE,"E25.6");var subQ3=sQuery(id+"F0.wireOp",EDGE,"E25.5");var subQ4=sQuery(id+"F0.wireOp",EDGE,"E25.4");var subQ5=sQuery(id+"F0.wireOp",EDGE,"E25.0");var subQ6=sQuery(id+"F0.wireOp",EDGE,"E25.2");var subQ7=sQuery(id+"F0.wireOp",EDGE,"E25.3");Q4=makeQuery(id+"F8.boolean.opBoolean","INTERSECT",EDGE,{"derivedFrom":[makeQuery(id+"F5.boolean.opBoolean","SPLIT",FACE,{"disambiguationData":[TD([makeQuery(id+"F2.opExtrude","SWEPT_FACE",FACE,{"disambiguationData":[OSD([subQ5])]})])],"derivedFrom":makeQuery(id+"F3.boolean.opBoolean","COPY",FACE,{"derivedFrom":makeQuery(id+"F3.opExtrude","CAP_FACE",FACE,{"disambiguationData":[OSD([subQ5,subQ1,subQ6,subQ7,subQ4,subQ3,subQ2,subQ0])],"isStart":false})})}),makeQuery(id+"F8.opExtrude","SWEPT_FACE",FACE,{"disambiguationData":[OSD([sQuery(id+"F7.wireOp",EDGE,"E75")])]})]});}
            var Q5;
            Q5=makeQuery(id+"F8.boolean.opBoolean","INTERSECT",EDGE,{"disambiguationData":[OD(0.0)],"derivedFrom":[makeQuery(id+"F5.opExtrude","SWEPT_FACE",FACE,{"disambiguationData":[OSD([sQuery(id+"F4.wireOp",EDGE,"E38")])]}),makeQuery(id+"F8.opExtrude","SWEPT_FACE",FACE,{"disambiguationData":[OSD([sQuery(id+"F7.wireOp",EDGE,"E75")])]})]});
            fillet(context, id + "F14", {"entities" : qUnion([Q0, Q1, Q2, Q3, Q4, Q5]), "radius" : 3 * mm, "tangentPropagation" : true, "allowEdgeOverflow" : false});
        }
        {
            var Q0;
            Q0=makeQuery(id+"F1.opExtrude","CAP_EDGE",EDGE,{"disambiguationData":[OSD([sQuery(id+"F0.wireOp",EDGE,"E1.bottom")])],"isStart":false});
            fillet(context, id + "F15", {"entities" : qUnion([Q0]), "radius" : 2 * mm, "tangentPropagation" : true, "allowEdgeOverflow" : false});
        }
        {
            var Q0;
            Q0=makeQuery(id+"F0.imprint","IMPRINT",FACE,{"disambiguationData":[TD([[makeQuery(id+"F0.imprint","IMPRINT",EDGE,{"derivedFrom":sQuery(id+"F0.wireOp",EDGE,"E28")}),-1.0]])]});
            var Q1;
            Q1=makeQuery(id+"FsijJI0vGDGG3KV_1.1.F0.imprint","IMPRINT",FACE,{"disambiguationData":[TD([[makeQuery(id+"FsijJI0vGDGG3KV_1.1.F0.imprint","IMPRINT",EDGE,{"derivedFrom":sQuery(id+"FsijJI0vGDGG3KV_1.1.F0.wireOp",EDGE,"E28")}),-1.0]])]});
            var Q2;
            Q2=makeQuery(id+"F0.imprint","IMPRINT",FACE,{"disambiguationData":[TD([[makeQuery(id+"F0.imprint","IMPRINT",EDGE,{"derivedFrom":sQuery(id+"F0.wireOp",EDGE,"E1.bottom")}),1.0]])]});
            var Q3;
            {var subQ0=sQuery(id+"F4.wireOp",EDGE,"E71.0.MirrorCS");var subQ1=sQuery(id+"F4.wireOp",EDGE,"E70.0.MirrorCS");var subQ2=sQuery(id+"F4.wireOp",EDGE,"E69.0.MirrorCS");var subQ3=sQuery(id+"F4.wireOp",EDGE,"E68.0.MirrorCS");var subQ4=sQuery(id+"F4.wireOp",EDGE,"E67.0.MirrorCS");var subQ5=sQuery(id+"F4.wireOp",EDGE,"E66.0.MirrorCS");var subQ6=sQuery(id+"F4.wireOp",EDGE,"E65.0.MirrorCS");var subQ7=sQuery(id+"F4.wireOp",EDGE,"E64.0.MirrorCS");var subQ8=sQuery(id+"F4.wireOp",EDGE,"E63.0.MirrorCS");var subQ9=sQuery(id+"F4.wireOp",EDGE,"E62.0.MirrorCS");var subQ10=sQuery(id+"F4.wireOp",EDGE,"E61.0.MirrorCS");var subQ11=sQuery(id+"F4.wireOp",EDGE,"E60.filletArc");var subQ12=sQuery(id+"F4.wireOp",EDGE,"E53");var subQ13=sQuery(id+"F4.wireOp",EDGE,"E51");var subQ14=sQuery(id+"F4.wireOp",EDGE,"E50");var subQ15=sQuery(id+"F4.wireOp",EDGE,"E49");var subQ16=sQuery(id+"F4.wireOp",EDGE,"E54");var subQ17=sQuery(id+"F4.wireOp",EDGE,"E55.filletArc");var subQ18=sQuery(id+"F4.wireOp",EDGE,"E56.filletArc");var subQ19=sQuery(id+"F4.wireOp",EDGE,"E57.filletArc");var subQ20=sQuery(id+"F4.wireOp",EDGE,"E58.filletArc");var subQ21=sQuery(id+"F4.wireOp",EDGE,"E59.filletArc");Q3=makeQuery(id+"F6.boolean.opBoolean","SPLIT",FACE,{"disambiguationData":[TD([makeQuery(id+"F5.opExtrude","SWEPT_FACE",FACE,{"disambiguationData":[OSD([subQ15])]})])],"derivedFrom":makeQuery(id+"F5.opExtrude","CAP_FACE",FACE,{"disambiguationData":[OSD([sQuery(id+"F4.wireOp",EDGE,"E35.0"),sQuery(id+"F4.wireOp",EDGE,"E36.0"),sQuery(id+"F4.wireOp",EDGE,"E37"),sQuery(id+"F4.wireOp",EDGE,"E38"),sQuery(id+"F4.wireOp",EDGE,"E41.filletArc"),sQuery(id+"F4.wireOp",EDGE,"E42.filletArc"),sQuery(id+"F4.wireOp",EDGE,"E43.filletArc"),sQuery(id+"F4.wireOp",EDGE,"E44.filletArc"),subQ15,subQ14,subQ13,subQ12,subQ16,subQ17,subQ18,subQ19,subQ20,subQ21,subQ11,subQ10,subQ9,subQ8,subQ7,subQ6,subQ5,subQ4,subQ3,subQ2,subQ1,subQ0])],"isStart":true})});}
            extrude(context, id + "F16", {"entities" : qUnion([Q0, Q1, Q2]), "endBound" : BoundingType.UP_TO_SURFACE, "depth" : 25 * mm, "endBoundEntityFace" : qUnion([Q3]), "offsetDistance" : 25 * mm});
        }
    });
